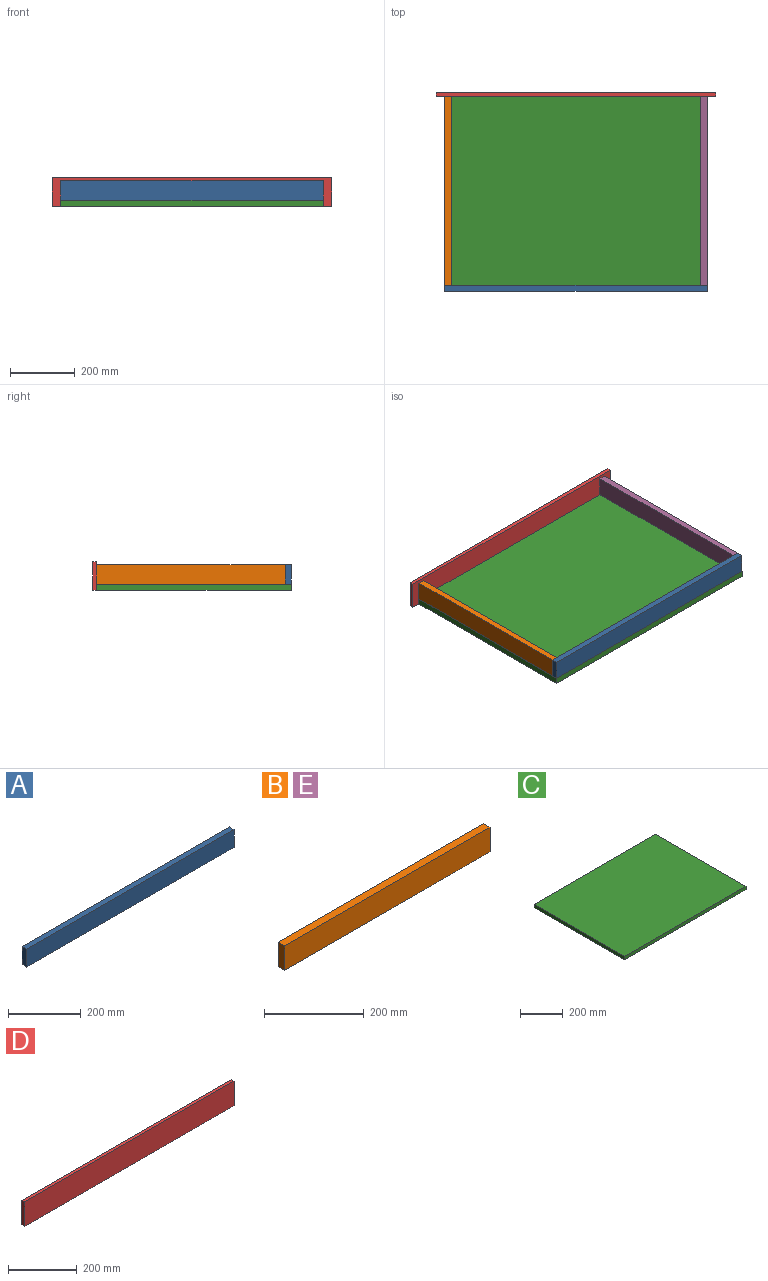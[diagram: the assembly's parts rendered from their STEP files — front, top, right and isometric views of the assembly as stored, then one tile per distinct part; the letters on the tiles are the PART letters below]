
ASSEMBLY  parts=5 mates=4
PART A: 6 faces, bbox 807x19x60 mm
  f0: plane 60x19mm, normal (-1,0,0), area 1140mm2, adj f1,f3,f4,f5
  f1: plane 807x19mm, normal (0,0,-1), area 15333mm2, adj f0,f2,f4,f5
  f2: plane 60x19mm, normal (1,0,0), area 1140mm2, adj f1,f3,f4,f5
  f3: plane 807x19mm, normal (0,0,1), area 15333mm2, adj f0,f2,f4,f5
  f4: plane 807x60mm, normal (0,-1,0), area 48420mm2, adj f0,f1,f2,f3
  f5: plane 807x60mm, normal (0,1,0), area 48420mm2, adj f0,f1,f2,f3
PART B: 6 faces, bbox 581x19x60 mm
  f0: plane 60x19mm, normal (-1,0,0), area 1140mm2, adj f1,f3,f4,f5
  f1: plane 581x19mm, normal (0,0,-1), area 11039mm2, adj f0,f2,f4,f5
  f2: plane 60x19mm, normal (1,0,0), area 1140mm2, adj f1,f3,f4,f5
  f3: plane 581x19mm, normal (0,0,1), area 11039mm2, adj f0,f2,f4,f5
  f4: plane 581x60mm, normal (0,-1,0), area 34860mm2, adj f0,f1,f2,f3
  f5: plane 581x60mm, normal (0,1,0), area 34860mm2, adj f0,f1,f2,f3
PART C: 6 faces, bbox 807x600x19 mm
  f0: plane 600x19mm, normal (-1,0,0), area 11400mm2, adj f1,f3,f4,f5
  f1: plane 807x19mm, normal (0,-1,0), area 15333mm2, adj f0,f2,f4,f5
  f2: plane 600x19mm, normal (1,0,0), area 11400mm2, adj f1,f3,f4,f5
  f3: plane 807x19mm, normal (0,1,0), area 15333mm2, adj f0,f2,f4,f5
  f4: plane 807x600mm, normal (0,0,1), area 484200mm2, adj f0,f1,f2,f3
  f5: plane 807x600mm, normal (0,0,-1), area 484200mm2, adj f0,f1,f2,f3
PART D: 6 faces, bbox 861x12x88 mm
  f0: plane 861x12mm, normal (0,0,1), area 10332mm2, adj f1,f3,f4,f5
  f1: plane 88x12mm, normal (-1,0,0), area 1056mm2, adj f0,f2,f4,f5
  f2: plane 861x12mm, normal (0,0,-1), area 10332mm2, adj f1,f3,f4,f5
  f3: plane 88x12mm, normal (1,0,0), area 1056mm2, adj f0,f2,f4,f5
  f4: plane 861x88mm, normal (0,-1,0), area 75768mm2, adj f0,f1,f2,f3
  f5: plane 861x88mm, normal (0,1,0), area 75768mm2, adj f0,f1,f2,f3
PART E: same geometry as B
PLACE A t=(-45.45,-39.38,11.47)mm
PLACE B rot(axis=(0,0,1),90deg) t=(-45.45,-39.38,11.47)mm
PLACE C t=(-45.45,-58.38,-7.53)mm
PLACE D t=(358.05,553.62,36.47)mm
PLACE E rot(axis=(0,0,1),90deg) t=(742.55,-39.38,11.47)mm
MATE fastened B.f1 <-> C.f4  axis (0,0,-1) through (-45.45,541.62,11.47)mm
MATE fastened C.f3 <-> D.f4  axis (0,1,0) through (358.05,541.62,-7.53)mm
MATE fastened A.f1 <-> C.f4  axis (0,0,-1) through (358.05,-58.38,11.47)mm
MATE fastened E.f1 <-> C.f4  axis (0,0,-1) through (761.55,541.62,11.47)mm
